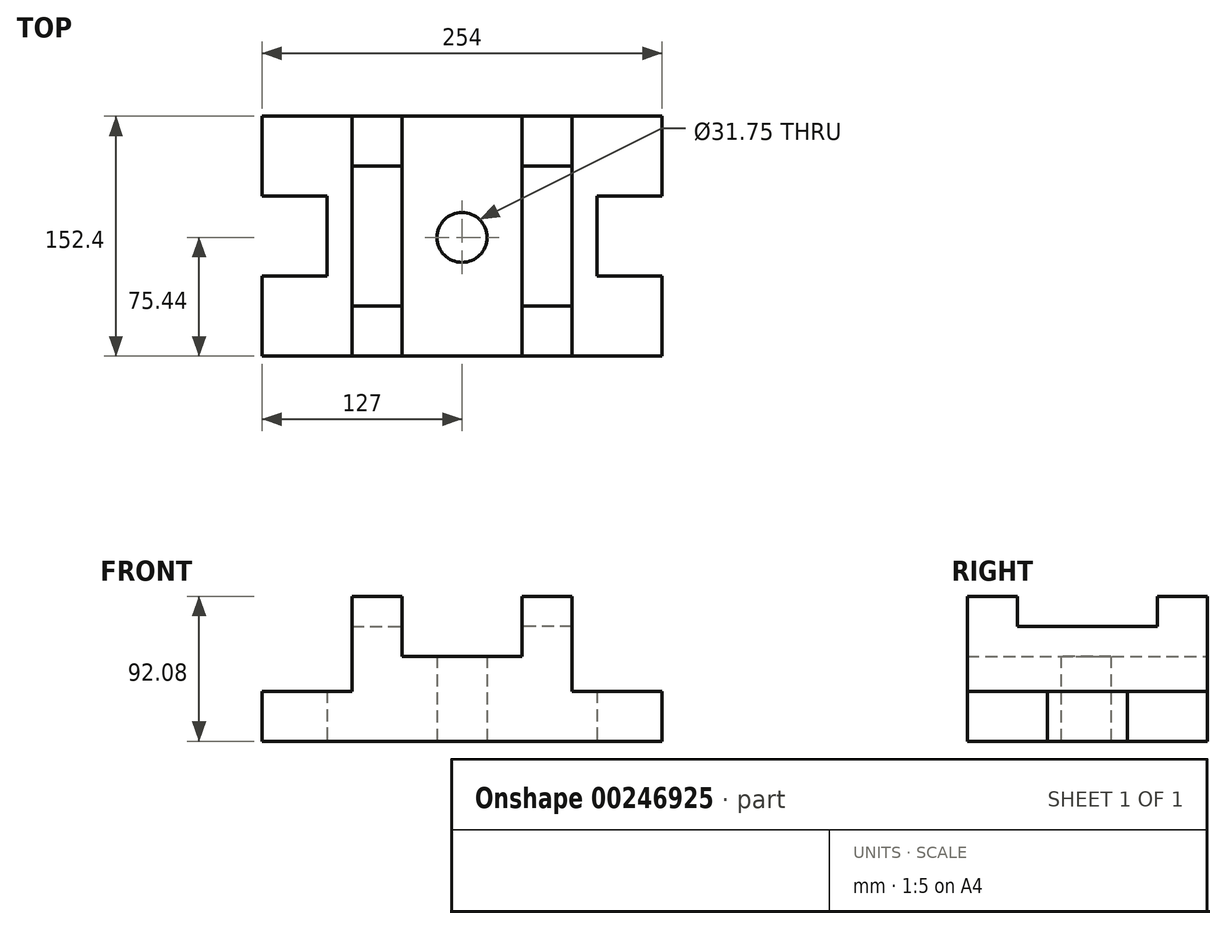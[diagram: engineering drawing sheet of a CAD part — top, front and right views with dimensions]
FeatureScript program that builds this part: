
annotation { "Feature Type Name" : "Feature", "Feature Type Description" : "" }
export const myFeature = defineFeature(function(context is Context, id is Id, definition is map)
    precondition{}
    {
        {
            var Q0;
            Q0=qCreatedBy(makeId("Top.planeOp"),FACE);
            var sketch = newSketch(context, id + "F0", { "sketchPlane" : qUnion([Q0])});
            skCircle(sketch, "E0", {"center": v(0, 0) * mm, "radius": 15.88 * mm});
            skLineSegment(sketch, "E1", {"start": v(0, 76.96) * mm, "end": v(127, 76.96) * mm});
            skLineSegment(sketch, "E2", {"start": v(127, 76.96) * mm, "end": v(127, 26.16) * mm});
            skLineSegment(sketch, "E3", {"start": v(127, 26.16) * mm, "end": v(85.73, 26.16) * mm});
            skLineSegment(sketch, "E4", {"start": v(85.73, 26.16) * mm, "end": v(85.73, -24.64) * mm});
            skLineSegment(sketch, "E5", {"start": v(85.73, -24.64) * mm, "end": v(127, -24.64) * mm});
            skLineSegment(sketch, "E6", {"start": v(127, -24.64) * mm, "end": v(127, -75.44) * mm});
            skLineSegment(sketch, "E7", {"start": v(38.1, -43.7) * mm, "end": v(69.85, -43.7) * mm});
            skLineSegment(sketch, "E8", {"start": v(69.85, 45.2) * mm, "end": v(38.1, 45.2) * mm});
            skLineSegment(sketch, "E9.MirrorCS", {"start": v(0, 76.96) * mm, "end": v(-127, 76.96) * mm});
            skLineSegment(sketch, "E10.MirrorCS", {"start": v(-69.85, 45.2) * mm, "end": v(-38.1, 45.2) * mm});
            skLineSegment(sketch, "E11.MirrorCS", {"start": v(-38.1, -43.7) * mm, "end": v(-69.85, -43.7) * mm});
            skLineSegment(sketch, "E12.MirrorCS", {"start": v(-127, -75.44) * mm, "end": v(0, -75.44) * mm});
            skLineSegment(sketch, "E13.MirrorCS", {"start": v(-69.85, 76.96) * mm, "end": v(-69.85, -75.44) * mm});
            skLineSegment(sketch, "E14.MirrorCS", {"start": v(-85.73, 26.16) * mm, "end": v(-85.73, -24.64) * mm});
            skLineSegment(sketch, "E15.MirrorCS", {"start": v(-127, 26.16) * mm, "end": v(-85.73, 26.16) * mm});
            skLineSegment(sketch, "E16.MirrorCS", {"start": v(-85.73, -24.64) * mm, "end": v(-127, -24.64) * mm});
            skLineSegment(sketch, "E17.MirrorCS", {"start": v(-127, 76.96) * mm, "end": v(-127, 26.16) * mm});
            skLineSegment(sketch, "E18.MirrorCS", {"start": v(-127, -24.64) * mm, "end": v(-127, -75.44) * mm});
            skLineSegment(sketch, "E19.MirrorCS", {"start": v(69.85, 76.96) * mm, "end": v(69.85, -75.44) * mm});
            skLineSegment(sketch, "E20.MirrorCS", {"start": v(38.1, -75.44) * mm, "end": v(38.1, 76.96) * mm});
            skLineSegment(sketch, "E21.MirrorCS", {"start": v(-38.1, -75.44) * mm, "end": v(-38.1, 76.96) * mm});
            skLineSegment(sketch, "E22.MirrorCS", {"start": v(127, -75.44) * mm, "end": v(0, -75.44) * mm});
            skSolve(sketch);
        }
        {
            var Q0;
            Q0=makeQuery(id+"F0.imprint","IMPRINT",FACE,{"disambiguationData":[TD([[makeQuery(id+"F0.imprint","IMPRINT",EDGE,{"derivedFrom":sQuery(id+"F0.wireOp",EDGE,"E0")}),-1.0]])]});
            extrude(context, id + "F1", {"entities" : qUnion([Q0]), "depth" : 53.97 * mm});
        }
        {
            var Q0;
            {var subQ5=sQuery(id+"F0.wireOp",EDGE,"E10.MirrorCS");Q0=makeQuery(id+"F0.imprint","IMPRINT",FACE,{"disambiguationData":[TD([[makeQuery(id+"F0.imprint","IMPRINT",EDGE,{"derivedFrom":subQ5}),1.0]])]});}
            var Q1;
            {var subQ0=sQuery(id+"F0.wireOp",EDGE,"E11.MirrorCS");Q1=makeQuery(id+"F0.imprint","IMPRINT",FACE,{"disambiguationData":[TD([[makeQuery(id+"F0.imprint","IMPRINT",EDGE,{"derivedFrom":subQ0}),1.0]])]});}
            var Q2;
            {var subQ5=sQuery(id+"F0.wireOp",EDGE,"E8");Q2=makeQuery(id+"F0.imprint","IMPRINT",FACE,{"disambiguationData":[TD([[makeQuery(id+"F0.imprint","IMPRINT",EDGE,{"derivedFrom":subQ5}),-1.0]])]});}
            var Q3;
            {var subQ0=sQuery(id+"F0.wireOp",EDGE,"E7");Q3=makeQuery(id+"F0.imprint","IMPRINT",FACE,{"disambiguationData":[TD([[makeQuery(id+"F0.imprint","IMPRINT",EDGE,{"derivedFrom":subQ0}),-1.0]])]});}
            extrude(context, id + "F2", {"entities" : qUnion([Q0, Q1, Q2, Q3]), "operationType" : NewBodyOperationType.ADD, "depth" : 92.07 * mm});
        }
        {
            var Q0;
            {var subQ0=sQuery(id+"F0.wireOp",EDGE,"E10.MirrorCS");Q0=makeQuery(id+"F0.imprint","IMPRINT",FACE,{"disambiguationData":[TD([[makeQuery(id+"F0.imprint","IMPRINT",EDGE,{"derivedFrom":subQ0}),-1.0]])]});}
            var Q1;
            {var subQ0=sQuery(id+"F0.wireOp",EDGE,"E7");Q1=makeQuery(id+"F0.imprint","IMPRINT",FACE,{"disambiguationData":[TD([[makeQuery(id+"F0.imprint","IMPRINT",EDGE,{"derivedFrom":subQ0}),1.0]])]});}
            extrude(context, id + "F3", {"entities" : qUnion([Q0, Q1]), "operationType" : NewBodyOperationType.ADD, "depth" : 73.02 * mm});
        }
        {
            var Q0;
            Q0=makeQuery(id+"F0.imprint","IMPRINT",FACE,{"disambiguationData":[TD([[makeQuery(id+"F0.imprint","IMPRINT",EDGE,{"derivedFrom":sQuery(id+"F0.wireOp",EDGE,"E14.MirrorCS")}),1.0]])]});
            var Q1;
            {var subQ4=sQuery(id+"F0.wireOp",EDGE,"E2");Q1=makeQuery(id+"F0.imprint","IMPRINT",FACE,{"disambiguationData":[TD([[makeQuery(id+"F0.imprint","IMPRINT",EDGE,{"derivedFrom":subQ4}),-1.0]])]});}
            extrude(context, id + "F4", {"entities" : qUnion([Q0, Q1]), "operationType" : NewBodyOperationType.ADD, "depth" : 31.75 * mm});
        }
    });
